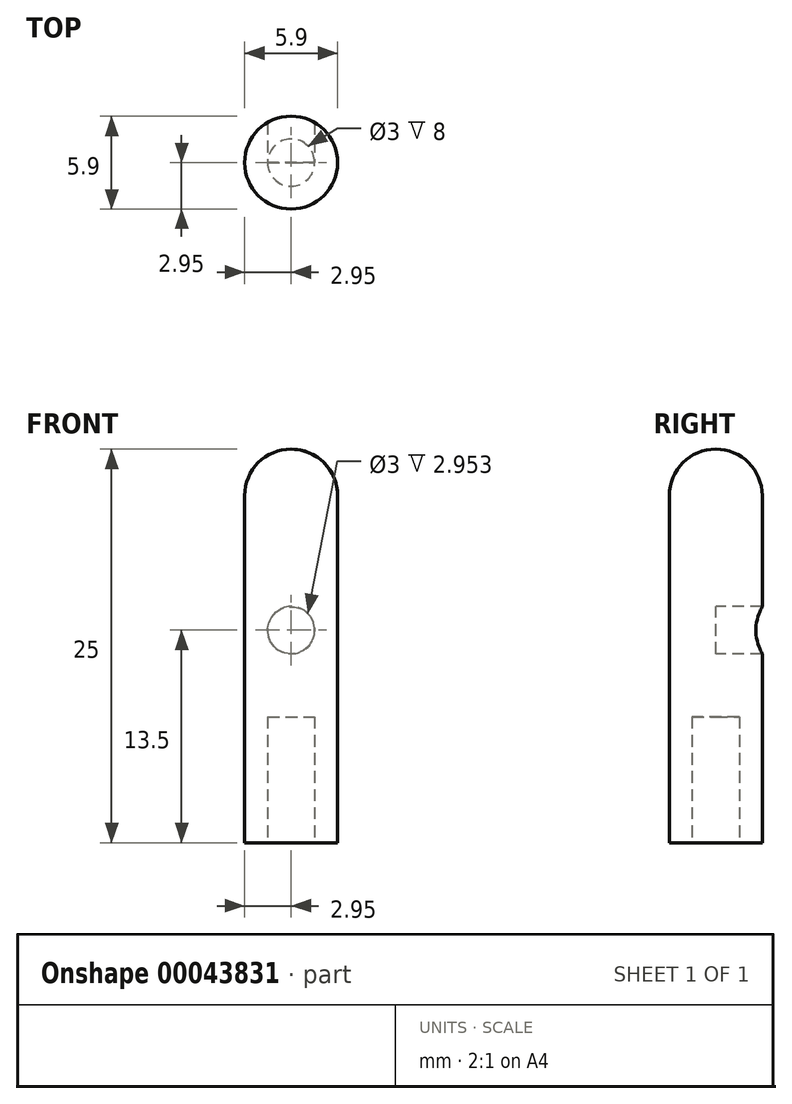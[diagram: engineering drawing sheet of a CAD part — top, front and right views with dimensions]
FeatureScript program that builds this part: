
annotation { "Feature Type Name" : "Feature", "Feature Type Description" : "" }
export const myFeature = defineFeature(function(context is Context, id is Id, definition is map)
    precondition{}
    {
        {
            var Q0;
            Q0=qCreatedBy(makeId("Front.planeOp"),FACE);
            var sketch = newSketch(context, id + "F0", { "sketchPlane" : qUnion([Q0])});
            skLineSegment(sketch, "E0", {"start": v(1.5, 0) * mm, "end": v(2.95, 0) * mm});
            skLineSegment(sketch, "E1", {"start": v(0, 8) * mm, "end": v(0, 25) * mm});
            skLineSegment(sketch, "E2.0", {"start": v(2.95, 0) * mm, "end": v(2.95, 22.05) * mm});
            skLineSegment(sketch, "E3.0", {"start": v(1.5, 0) * mm, "end": v(1.5, 8) * mm});
            skLineSegment(sketch, "E4.0", {"start": v(0, 8) * mm, "end": v(1.5, 8) * mm});
            skArc(sketch, "E5", {"start": v(2.95, 22.05) * mm, "mid": v(2.09, 24.14) * mm, "end": v(0, 25) * mm});
            skSolve(sketch);
        }
        {
            var Q0;
            Q0 = qSketchRegion(id + "F0", true);
            var Q1;
            Q1=sQuery(id+"F0.wireOp",EDGE,"E1");
            revolve(context, id + "F1", {"entities" : qUnion([Q0]), "axis" : qUnion([Q1]), "revolveType" : RevolveType.FULL});
        }
        {
            var Q0;
            Q0=qCreatedBy(makeId("Front.planeOp"),FACE);
            var sketch = newSketch(context, id + "F2", { "sketchPlane" : qUnion([Q0])});
            skLineSegment(sketch, "E6", {"start": v(0, 0) * mm, "end": v(10.19, 0) * mm});
            skLineSegment(sketch, "E7.0", {"start": v(0, 13.5) * mm, "end": v(10.19, 13.5) * mm});
            skCircle(sketch, "E8", {"center": v(0, 13.5) * mm, "radius": 1.5 * mm});
            skSolve(sketch);
        }
        {
            var Q0;
            Q0 = qSketchRegion(id + "F2", true);
            extrude(context, id + "F3", {"entities" : qUnion([Q0]), "operationType" : NewBodyOperationType.REMOVE, "oppositeDirection" : true, "depth" : 25 * mm});
        }
    });
